# Revit family: Haworth_BeHold_Modular_AttachedStorage
name_source: partatom
category: Furniture Systems
revit_build: Autodesk Revit 2018 (Build: 20170223_1515(x64)
units: mm (PartAtom-declared; Revit-internal decimal feet)

## family parameters
Always vertical = Yes
Cut with Voids When Loaded = No
OmniClass Number = 23.40.70.14.64.21
OmniClass Title = Systems Furniture
Part Type = Normal
Room Calculation Point = No
Round Connector Dimension = Use Diameter
Shared = No
Work Plane-Based = No

## types (8) — shared parameters
16d Leg = No
Actual D/T Leg Control = No
Actual Depth = 24"
Assembly Code = E2020200
Case Thickness = 3/4"
Classic Pull = No
Classic Pull Length = 8"
Cresent Pull = No
Custom Size = No
Depth = 24"
Description = Haworth - Be_Hold - Attached Storage
Door Width = 17 7/8"
Double Unit Leg = No
Glide Finish = Haworth _ Polymer _ Slate
Leg Height = 6"
Linear Pull = No
Linear Pull Length = 7 33/256"
Manufacturer = Haworth
Max. Depth = 24"
Max. Height = 42"
Min. Depth = 16"
Min. Height = 22"
Model = Haworth Be_Hold
No Pull = No
Revision Number = 1
Shelf 1 Offset = 12 149/256"
Single Unit Leg = Yes
Size = Verify Final Dim. w/ Haworth
Standard Depths = 16, 24 in.
Sustainability Info = https://www.haworth.com
Top Thickness = 3/4"
Triple Unit Leg = No
URL = www.haworth.com
URL - Product = https://www.haworth.com
Warranty = http://www.haworth.com
Wing Pull = Yes
Wing Pull Length = 8 5/16"
With Lock = Yes

## per-type parameters (varying)
- 2H - Double Doors - Proud Back - 24d 36w: Actual Height=28"; Actual Single Leg Control=No; Actual Width=36"; Back Case Back Control=0"; Back Case Side Control=0"; Bottom Case Offset=1/2"; Door Height=26 59/128"; Double Doors=Yes; Glide Control=Yes; Inset Style=No; Left Door Control=Yes; Max. Width=36"; Min. Width=24"; Normal Storage Height=28"; One and One Half High=No; Open=No; Proud Style=Yes; Right Door Control=Yes; Shelf 2 Control=No; Shelf 2 Offset=12 149/256"; Side Case Back Control=3/4"; Side Case Front Control=3/4"; Single Door=No; Standard Widths=24, 30, 36 in.; Three High=No; Top Case Back Control=0"; Top Case Front Control=0"; Two High=Yes; Width=36"; With Leg=No
- 3H - Double Doors - Inset Back - 24d 36w: Actual Height=42"; Actual Single Leg Control=No; Actual Width=36"; Back Case Back Control=3/16"; Back Case Side Control=3/4"; Bottom Case Offset=1/2"; Door Height=40 59/128"; Double Doors=Yes; Glide Control=Yes; Inset Style=Yes; Left Door Control=Yes; Max. Width=36"; Min. Width=24"; Normal Storage Height=42"; One and One Half High=No; Open=No; Proud Style=No; Right Door Control=Yes; Shelf 2 Control=Yes; Shelf 2 Offset=25 13/16"; Side Case Back Control=0"; Side Case Front Control=3/4"; Single Door=No; Standard Widths=24, 30, 36 in.; Three High=Yes; Top Case Back Control=3/16"; Top Case Front Control=0"; Two High=No; Width=36"; With Leg=No
- 2H - Single Door - Proud Back - 24d 18w: Actual Height=28"; Actual Single Leg Control=No; Actual Width=18"; Back Case Back Control=0"; Back Case Side Control=0"; Bottom Case Offset=1/2"; Door Height=26 59/128"; Double Doors=No; Glide Control=Yes; Inset Style=No; Left Door Control=No; Max. Width=18"; Min. Width=18"; Normal Storage Height=28"; One and One Half High=No; Open=No; Proud Style=Yes; Right Door Control=Yes; Shelf 2 Control=No; Shelf 2 Offset=12 149/256"; Side Case Back Control=3/4"; Side Case Front Control=3/4"; Single Door=Yes; Standard Widths=18 in.; Three High=No; Top Case Back Control=0"; Top Case Front Control=0"; Two High=Yes; Width=18"; With Leg=No
- 3H - Single Door - Inset Back - 24d 18w: Actual Height=42"; Actual Single Leg Control=No; Actual Width=18"; Back Case Back Control=3/16"; Back Case Side Control=3/4"; Bottom Case Offset=1/2"; Door Height=40 59/128"; Double Doors=No; Glide Control=Yes; Inset Style=Yes; Left Door Control=No; Max. Width=18"; Min. Width=18"; Normal Storage Height=42"; One and One Half High=No; Open=No; Proud Style=No; Right Door Control=Yes; Shelf 2 Control=Yes; Shelf 2 Offset=25 13/16"; Side Case Back Control=0"; Side Case Front Control=3/4"; Single Door=Yes; Standard Widths=18 in.; Three High=Yes; Top Case Back Control=3/16"; Top Case Front Control=0"; Two High=No; Width=18"; With Leg=No
- 2H - Open - Proud Back - 24d 36w: Actual Height=28"; Actual Single Leg Control=No; Actual Width=36"; Back Case Back Control=0"; Back Case Side Control=0"; Bottom Case Offset=1/2"; Door Height=26 59/128"; Double Doors=No; Glide Control=Yes; Inset Style=No; Left Door Control=No; Max. Width=36"; Min. Width=18"; Normal Storage Height=28"; One and One Half High=No; Open=Yes; Proud Style=Yes; Right Door Control=No; Shelf 2 Control=No; Shelf 2 Offset=12 149/256"; Side Case Back Control=3/4"; Side Case Front Control=0"; Single Door=No; Standard Widths=18, 24, 30, 36 in.; Three High=No; Top Case Back Control=0"; Top Case Front Control=2 1/4"; Two High=Yes; Width=36"; With Leg=No
- 1.5H - Open - Inset Back - 24d 36w: Actual Height=22"; Actual Single Leg Control=No; Actual Width=36"; Back Case Back Control=3/16"; Back Case Side Control=3/4"; Bottom Case Offset=1/2"; Door Height=20 59/128"; Double Doors=No; Glide Control=Yes; Inset Style=Yes; Left Door Control=No; Max. Width=36"; Min. Width=18"; Normal Storage Height=22"; One and One Half High=Yes; Open=Yes; Proud Style=No; Right Door Control=No; Shelf 2 Control=No; Shelf 2 Offset=12 149/256"; Side Case Back Control=0"; Side Case Front Control=0"; Single Door=No; Standard Widths=18, 24, 30, 36 in.; Three High=No; Top Case Back Control=3/16"; Top Case Front Control=2 1/4"; Two High=No; Width=36"; With Leg=No
- 1.5H - Open - Inset Back - 24d 36w - With Leg: Actual Height=28"; Actual Single Leg Control=Yes; Actual Width=36"; Back Case Back Control=3/16"; Back Case Side Control=3/4"; Bottom Case Offset=6"; Door Height=20 123/128"; Double Doors=No; Glide Control=No; Inset Style=Yes; Left Door Control=No; Max. Width=36"; Min. Width=18"; Normal Storage Height=22"; One and One Half High=Yes; Open=Yes; Proud Style=No; Right Door Control=No; Shelf 2 Control=No; Shelf 2 Offset=12 149/256"; Side Case Back Control=0"; Side Case Front Control=0"; Single Door=No; Standard Widths=18, 24, 30, 36 in.; Three High=No; Top Case Back Control=3/16"; Top Case Front Control=2 1/4"; Two High=No; Width=36"; With Leg=Yes
- 2H - Double Doors - Proud Back - 24d 36w - With Leg: Actual Height=34"; Actual Single Leg Control=Yes; Actual Width=36"; Back Case Back Control=0"; Back Case Side Control=0"; Bottom Case Offset=6"; Door Height=26 123/128"; Double Doors=Yes; Glide Control=No; Inset Style=No; Left Door Control=Yes; Max. Width=36"; Min. Width=24"; Normal Storage Height=28"; One and One Half High=No; Open=No; Proud Style=Yes; Right Door Control=Yes; Shelf 2 Control=No; Shelf 2 Offset=12 149/256"; Side Case Back Control=3/4"; Side Case Front Control=3/4"; Single Door=No; Standard Widths=24, 30, 36 in.; Three High=No; Top Case Back Control=0"; Top Case Front Control=0"; Two High=Yes; Width=36"; With Leg=Yes

## geometry (parser evidence)
native form markers: Sweep x14
no freeform markers — native parametric forms only
